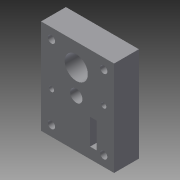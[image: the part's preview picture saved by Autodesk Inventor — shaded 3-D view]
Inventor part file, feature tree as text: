
AUTODESK INVENTOR PART (.ipt)
format: ipt  version: 2015 (Build 190159000, 159)  size: 169,472 bytes
history: native  units: mm
features: chamfer x6, hole x4, extrude x1, sketch x1
ambient origin geometry x8: Origin, YZ Plane, XZ Plane, XY Plane, X Axis, Y Axis, Z Axis, Center Point
bodies: Solid1 (feature_tree)
feature tree (12):
  extrude  "Extrusion1"  Depth=23.5mm
  hole  "Hole1"  [1 undecoded]
  hole  "Hole2"  [1 undecoded]
  hole  "Hole3"  [1 undecoded]
  hole  "Hole4"  [1 undecoded]
  chamfer  "Chamfer1"  Distance=23.5mm
  chamfer  "Chamfer2"  Distance=70.5mm
  chamfer  "Chamfer3"  Distance=21.625mm
  chamfer  "Chamfer4"  Distance=70.5mm
  chamfer  "Chamfer5"  Distance=91.5mm
  chamfer  "Chamfer6"  Distance=10.0mm
  sketch  "Sketch1"  dims[d0=21.0mm d1=23.5mm d2=10.5mm d3=11.75mm d5=23.5mm d6=5.0mm d7=23.5mm d9=70.5mm d40=21.625mm d41=70.5mm d42=91.5mm d43=10.0mm d44=10.0mm d45=7.0mm d46=10.0mm d47=10.0mm d48=90.0deg d50=7.0mm d51=10.0mm d52=10.0mm d53=7.0mm d54=10.0mm d55=10.0mm d56=7.0mm d60=30.0mm d61=30.0mm d62=5.0mm d63=5.0mm d64=14.0mm d65=24.0mm d66=0.0mm d67=10.0mm d68=10.0mm d69=3.0mm d70=6.0mm d71=10.0mm d72=7.0mm d73=90.0deg d74=8.0mm d75=20.594885mm d76=10.0mm d77=10.0mm d78=3.0mm d79=6.0mm d80=10.0mm d81=7.0mm d82=90.0deg d83=8.0mm d84=20.594885mm d85=10.0mm d86=10.0mm d87=3.0mm d88=6.0mm d89=10.0mm d90=7.0mm d91=90.0deg d92=8.0mm d93=20.594885mm d94=10.0mm d95=10.0mm d96=3.0mm d97=6.0mm d98=10.0mm d99=7.0mm d100=90.0deg d101=8.0mm d102=20.594885mm d103=0.698mm d104=20.0mm d105=0.349066mm d106=0.698mm d107=20.0mm d108=0.349066mm d109=0.698mm d110=20.0mm d111=0.349066mm d112=20.0mm d113=0.698mm d114=0.349066mm d115=0.698mm d116=20.0mm d117=0.349066mm d118=0.698mm d119=20.0mm d120=0.349066mm d121=34.0mm]
note: 4 required parameter values undecoded (feature->parameter linkage not recoverable at this tier; creation-order binding heuristic only, values carry confidence <= 0.55)
